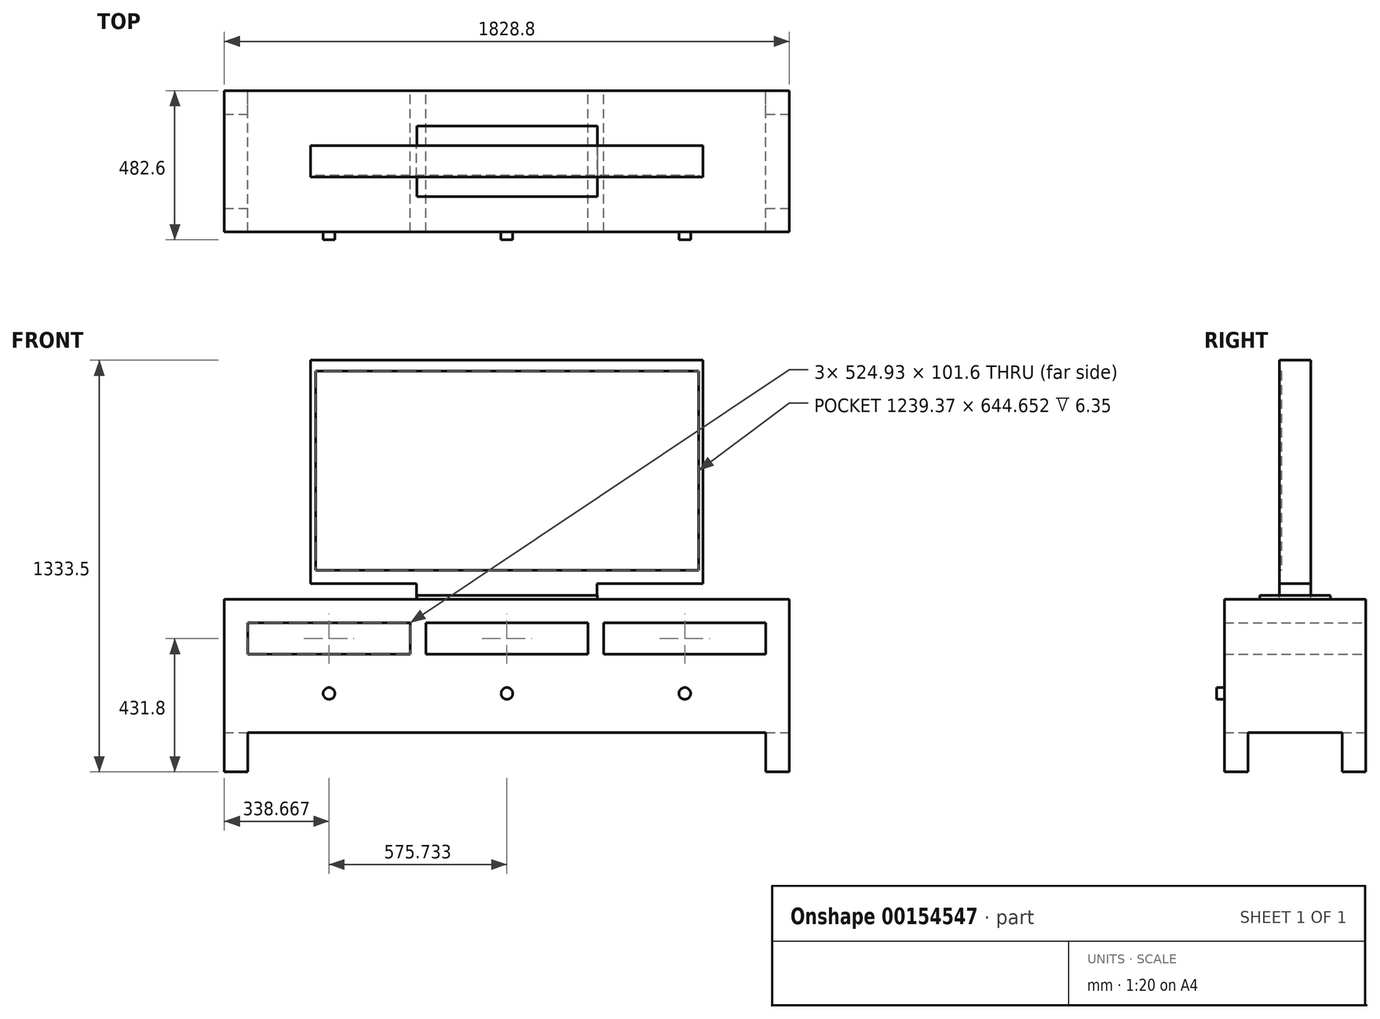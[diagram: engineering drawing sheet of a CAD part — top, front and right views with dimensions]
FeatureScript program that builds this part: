
annotation { "Feature Type Name" : "Feature", "Feature Type Description" : "" }
export const myFeature = defineFeature(function(context is Context, id is Id, definition is map)
    precondition{}
    {
        {
            var Q0;
            Q0=qCreatedBy(makeId("Front.planeOp"),FACE);
            var sketch = newSketch(context, id + "F0", { "sketchPlane" : qUnion([Q0])});
            skLineSegment(sketch, "E0", {"start": v(0, 0) * mm, "end": v(0, 558.8) * mm});
            skLineSegment(sketch, "E1", {"start": v(0, 558.8) * mm, "end": v(1828.8, 558.8) * mm});
            skLineSegment(sketch, "E2", {"start": v(1828.8, 558.8) * mm, "end": v(1828.8, 0) * mm});
            skLineSegment(sketch, "E3", {"start": v(1828.8, 0) * mm, "end": v(0, 0) * mm});
            skLineSegment(sketch, "E4", {"start": v(0, 127) * mm, "end": v(1828.8, 127) * mm});
            skPoint(sketch, "E4.endSnap0", {"position": v(1828.8, 279.4) * mm});
            skLineSegment(sketch, "E5", {"start": v(76.2, 127) * mm, "end": v(76.2, 0) * mm});
            skLineSegment(sketch, "E6", {"start": v(1752.6, 127) * mm, "end": v(1752.6, 0) * mm});
            skLineSegment(sketch, "E7.bottom", {"start": v(76.2, 482.6) * mm, "end": v(1752.6, 482.6) * mm});
            skLineSegment(sketch, "E7.top", {"start": v(76.2, 381) * mm, "end": v(1752.6, 381) * mm});
            skLineSegment(sketch, "E7.left", {"start": v(76.2, 482.6) * mm, "end": v(76.2, 381) * mm});
            skLineSegment(sketch, "E7.right", {"start": v(1752.6, 482.6) * mm, "end": v(1752.6, 381) * mm});
            skLineSegment(sketch, "E8", {"start": v(601.13, 482.6) * mm, "end": v(601.13, 381) * mm});
            skLineSegment(sketch, "E9", {"start": v(651.93, 482.6) * mm, "end": v(651.93, 381) * mm});
            skLineSegment(sketch, "E10", {"start": v(1176.87, 482.6) * mm, "end": v(1176.87, 381) * mm});
            skLineSegment(sketch, "E11", {"start": v(1227.67, 482.6) * mm, "end": v(1227.67, 381) * mm});
            skLineSegment(sketch, "E12", {"start": v(76.2, 431.8) * mm, "end": v(601.13, 431.8) * mm, "construction": true});
            skLineSegment(sketch, "E13", {"start": v(601.13, 431.8) * mm, "end": v(651.93, 431.8) * mm, "construction": true});
            skLineSegment(sketch, "E14", {"start": v(651.93, 431.8) * mm, "end": v(1176.87, 431.8) * mm, "construction": true});
            skLineSegment(sketch, "E15", {"start": v(1176.87, 431.8) * mm, "end": v(1227.67, 431.8) * mm, "construction": true});
            skLineSegment(sketch, "E16", {"start": v(1227.67, 431.8) * mm, "end": v(1752.6, 431.8) * mm, "construction": true});
            skLineSegment(sketch, "E17.bottom", {"start": v(279.4, 609.6) * mm, "end": v(1549.4, 609.6) * mm});
            skLineSegment(sketch, "E17.top", {"start": v(279.4, 1333.5) * mm, "end": v(1549.4, 1333.5) * mm});
            skLineSegment(sketch, "E17.left", {"start": v(279.4, 609.6) * mm, "end": v(279.4, 1333.5) * mm});
            skLineSegment(sketch, "E17.right", {"start": v(1549.4, 609.6) * mm, "end": v(1549.4, 1333.5) * mm});
            skLineSegment(sketch, "E18", {"start": v(622.3, 609.6) * mm, "end": v(622.3, 558.8) * mm});
            skLineSegment(sketch, "E19", {"start": v(1206.5, 609.6) * mm, "end": v(1206.5, 558.8) * mm});
            skLineSegment(sketch, "E20", {"start": v(914.4, 609.6) * mm, "end": v(914.4, 558.8) * mm, "construction": true});
            skLineSegment(sketch, "E21", {"start": v(622.3, 584.2) * mm, "end": v(914.4, 584.2) * mm, "construction": true});
            skLineSegment(sketch, "E22", {"start": v(914.4, 584.2) * mm, "end": v(1206.5, 584.2) * mm, "construction": true});
            skSolve(sketch);
        }
        {
            var Q0;
            {var subQ20=sQuery(id+"F0.wireOp",EDGE,"E1");Q0=makeQuery(id+"F0.imprint","IMPRINT",FACE,{"disambiguationData":[TD([[makeQuery(id+"F0.imprint","IMPRINT",EDGE,{"derivedFrom":subQ20}),-1.0]])]});}
            var Q1;
            {var subQ5=sQuery(id+"F0.wireOp",EDGE,"E5");Q1=makeQuery(id+"F0.imprint","IMPRINT",FACE,{"disambiguationData":[TD([[makeQuery(id+"F0.imprint","IMPRINT",EDGE,{"derivedFrom":subQ5}),-1.0]])]});}
            var Q2;
            {var subQ5=sQuery(id+"F0.wireOp",EDGE,"E6");Q2=makeQuery(id+"F0.imprint","IMPRINT",FACE,{"disambiguationData":[TD([[makeQuery(id+"F0.imprint","IMPRINT",EDGE,{"derivedFrom":subQ5}),1.0]])]});}
            var Q3;
            {var subQ0=sQuery(id+"F0.wireOp",EDGE,"E8");Q3=makeQuery(id+"F0.imprint","IMPRINT",FACE,{"disambiguationData":[TD([[makeQuery(id+"F0.imprint","IMPRINT",EDGE,{"derivedFrom":subQ0}),1.0]])]});}
            var Q4;
            {var subQ0=sQuery(id+"F0.wireOp",EDGE,"E10");Q4=makeQuery(id+"F0.imprint","IMPRINT",FACE,{"disambiguationData":[TD([[makeQuery(id+"F0.imprint","IMPRINT",EDGE,{"derivedFrom":subQ0}),1.0]])]});}
            extrude(context, id + "F1", {"entities" : qUnion([Q0, Q1, Q2, Q3, Q4]), "depth" : 457.2 * mm, "symmetric" : true});
        }
        {
            var Q0;
            Q0=makeQuery(id+"F1.opExtrude","SWEPT_FACE",FACE,{"disambiguationData":[OSD([sQuery(id+"F0.wireOp",EDGE,"E2")])]});
            var sketch = newSketch(context, id + "F2", { "sketchPlane" : qUnion([Q0])});
            skLineSegment(sketch, "E23.bottom", {"start": v(-152.4, 0) * mm, "end": v(152.4, 0) * mm});
            skLineSegment(sketch, "E23.top", {"start": v(-152.4, 127) * mm, "end": v(152.4, 127) * mm});
            skLineSegment(sketch, "E23.left", {"start": v(-152.4, 0) * mm, "end": v(-152.4, 127) * mm});
            skLineSegment(sketch, "E23.right", {"start": v(152.4, 0) * mm, "end": v(152.4, 127) * mm});
            skSolve(sketch);
        }
        {
            var Q0;
            Q0=makeQuery(id+"F2.imprint","IMPRINT",FACE,{"disambiguationData":[TD([[makeQuery(id+"F2.imprint","IMPRINT",EDGE,{"derivedFrom":sQuery(id+"F2.wireOp",EDGE,"E23.bottom")}),1.0]])]});
            extrude(context, id + "F3", {"entities" : qUnion([Q0]), "operationType" : NewBodyOperationType.REMOVE, "endBound" : BoundingType.THROUGH_ALL, "oppositeDirection" : true, "depth" : 30.48 * mm});
        }
        {
            var Q0;
            Q0=makeQuery(id+"F0.imprint","IMPRINT",FACE,{"disambiguationData":[TD([[makeQuery(id+"F0.imprint","IMPRINT",EDGE,{"derivedFrom":sQuery(id+"F0.wireOp",EDGE,"E17.top")}),-1.0]])]});
            var Q1;
            {var subQ0=sQuery(id+"F0.wireOp",EDGE,"E18");Q1=makeQuery(id+"F0.imprint","IMPRINT",FACE,{"disambiguationData":[TD([[makeQuery(id+"F0.imprint","IMPRINT",EDGE,{"derivedFrom":subQ0}),1.0]])]});}
            extrude(context, id + "F4", {"entities" : qUnion([Q0, Q1]), "operationType" : NewBodyOperationType.ADD, "depth" : 101.6 * mm, "symmetric" : true});
        }
        {
            var Q0;
            Q0=makeQuery(id+"F1.opExtrude","SWEPT_FACE",FACE,{"disambiguationData":[OSD([sQuery(id+"F0.wireOp",EDGE,"E1")])]});
            var sketch = newSketch(context, id + "F5", { "sketchPlane" : qUnion([Q0])});
            skLineSegment(sketch, "E24.bottom", {"start": v(1207.11, 114.3) * mm, "end": v(622.91, 114.3) * mm});
            skLineSegment(sketch, "E24.top", {"start": v(1207.11, -114.3) * mm, "end": v(622.91, -114.3) * mm});
            skLineSegment(sketch, "E24.left", {"start": v(1207.11, 114.3) * mm, "end": v(1207.11, -114.3) * mm});
            skLineSegment(sketch, "E24.right", {"start": v(622.91, 114.3) * mm, "end": v(622.91, -114.3) * mm});
            skPoint(sketch, "E24.middle", {"position": v(915.01, 0) * mm});
            skSolve(sketch);
        }
        {
            var Q0;
            Q0 = qSketchRegion(id + "F5", true);
            extrude(context, id + "F6", {"entities" : qUnion([Q0]), "operationType" : NewBodyOperationType.ADD, "depth" : 12.7 * mm});
        }
        {
            var Q0;
            Q0=makeQuery(id+"F1.opExtrude","CAP_FACE",FACE,{"disambiguationData":[OSD([sQuery(id+"F0.wireOp",EDGE,"E0"),sQuery(id+"F0.wireOp",EDGE,"E1"),sQuery(id+"F0.wireOp",EDGE,"E2"),sQuery(id+"F0.wireOp",EDGE,"E3"),sQuery(id+"F0.wireOp",EDGE,"E4"),sQuery(id+"F0.wireOp",EDGE,"E5"),sQuery(id+"F0.wireOp",EDGE,"E6"),sQuery(id+"F0.wireOp",EDGE,"E7.bottom"),sQuery(id+"F0.wireOp",EDGE,"E7.top"),sQuery(id+"F0.wireOp",EDGE,"E7.left"),sQuery(id+"F0.wireOp",EDGE,"E7.right"),sQuery(id+"F0.wireOp",EDGE,"E8"),sQuery(id+"F0.wireOp",EDGE,"E9"),sQuery(id+"F0.wireOp",EDGE,"E10"),sQuery(id+"F0.wireOp",EDGE,"E11")])],"isStart":false});
            var sketch = newSketch(context, id + "F7", { "sketchPlane" : qUnion([Q0])});
            skLineSegment(sketch, "E25", {"start": v(338.67, 381) * mm, "end": v(338.67, 127) * mm, "construction": true});
            skLineSegment(sketch, "E26", {"start": v(914.4, 381) * mm, "end": v(914.4, 127) * mm, "construction": true});
            skLineSegment(sketch, "E27", {"start": v(1490.13, 381) * mm, "end": v(1490.13, 127) * mm, "construction": true});
            skCircle(sketch, "E28", {"center": v(338.67, 254) * mm, "radius": 19.05 * mm});
            skCircle(sketch, "E29", {"center": v(914.4, 254) * mm, "radius": 19.05 * mm});
            skCircle(sketch, "E30", {"center": v(1490.13, 254) * mm, "radius": 19.05 * mm});
            skSolve(sketch);
        }
        {
            var Q0;
            Q0=makeQuery(id+"F7.imprint","IMPRINT",FACE,{"disambiguationData":[TD([[makeQuery(id+"F7.imprint","IMPRINT",EDGE,{"derivedFrom":sQuery(id+"F7.wireOp",EDGE,"E28")}),1.0]])]});
            var Q1;
            Q1=makeQuery(id+"F7.imprint","IMPRINT",FACE,{"disambiguationData":[TD([[makeQuery(id+"F7.imprint","IMPRINT",EDGE,{"derivedFrom":sQuery(id+"F7.wireOp",EDGE,"E29")}),1.0]])]});
            var Q2;
            Q2=makeQuery(id+"F7.imprint","IMPRINT",FACE,{"disambiguationData":[TD([[makeQuery(id+"F7.imprint","IMPRINT",EDGE,{"derivedFrom":sQuery(id+"F7.wireOp",EDGE,"E30")}),1.0]])]});
            extrude(context, id + "F8", {"entities" : qUnion([Q0, Q1, Q2]), "operationType" : NewBodyOperationType.ADD, "depth" : 25.4 * mm});
        }
        {
            var Q0;
            Q0=makeQuery(id+"F4.opExtrude","CAP_FACE",FACE,{"disambiguationData":[OSD([sQuery(id+"F0.wireOp",EDGE,"E1"),sQuery(id+"F0.wireOp",EDGE,"E17.bottom"),sQuery(id+"F0.wireOp",EDGE,"E17.top"),sQuery(id+"F0.wireOp",EDGE,"E17.left"),sQuery(id+"F0.wireOp",EDGE,"E17.right"),sQuery(id+"F0.wireOp",EDGE,"E18"),sQuery(id+"F0.wireOp",EDGE,"E19")])],"isStart":false});
            var sketch = newSketch(context, id + "F9", { "sketchPlane" : qUnion([Q0])});
            skLineSegment(sketch, "E31.bottom", {"start": v(295.02, 1297.95) * mm, "end": v(1534.4, 1297.95) * mm});
            skLineSegment(sketch, "E31.top", {"start": v(295.02, 653.3) * mm, "end": v(1534.4, 653.3) * mm});
            skLineSegment(sketch, "E31.left", {"start": v(295.02, 1297.95) * mm, "end": v(295.02, 653.3) * mm});
            skLineSegment(sketch, "E31.right", {"start": v(1534.4, 1297.95) * mm, "end": v(1534.4, 653.3) * mm});
            skLineSegment(sketch, "E32", {"start": v(295.02, 1297.95) * mm, "end": v(1534.4, 653.3) * mm, "construction": true});
            skLineSegment(sketch, "E33", {"start": v(914.7, 653.3) * mm, "end": v(914.7, 571.5) * mm, "construction": true});
            skSolve(sketch);
        }
        {
            var Q0;
            Q0 = qSketchRegion(id + "F9", true);
            extrude(context, id + "F10", {"entities" : qUnion([Q0]), "operationType" : NewBodyOperationType.REMOVE, "oppositeDirection" : true, "depth" : 6.35 * mm});
        }
    });
